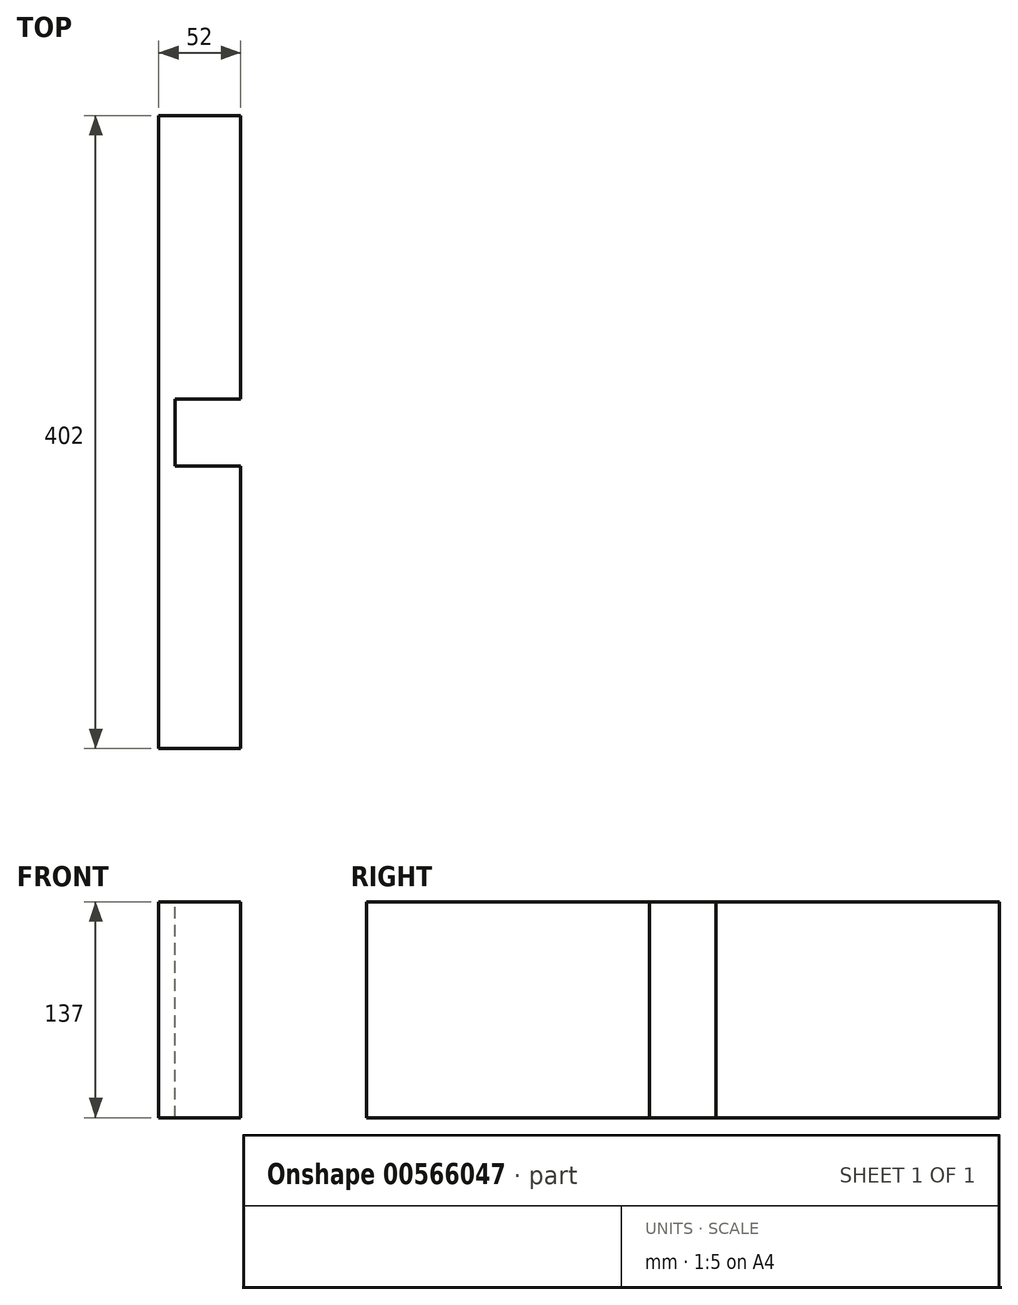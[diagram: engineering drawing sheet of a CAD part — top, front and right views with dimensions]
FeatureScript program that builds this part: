
annotation { "Feature Type Name" : "Feature", "Feature Type Description" : "" }
export const myFeature = defineFeature(function(context is Context, id is Id, definition is map)
    precondition{}
    {
        {
            var Q0;
            Q0=qCreatedBy(makeId("Top.planeOp"),FACE);
            var sketch = newSketch(context, id + "F0", { "sketchPlane" : qUnion([Q0])});
            skLineSegment(sketch, "E0.bottom", {"start": v(-95.63, 172.8) * mm, "end": v(-43.63, 172.8) * mm});
            skLineSegment(sketch, "E0.top", {"start": v(-95.63, -229.2) * mm, "end": v(-43.63, -229.2) * mm});
            skLineSegment(sketch, "E0.left", {"start": v(-95.63, 172.8) * mm, "end": v(-95.63, -229.2) * mm});
            skLineSegment(sketch, "E0.right", {"start": v(-43.63, 172.8) * mm, "end": v(-43.63, -229.2) * mm});
            skSolve(sketch);
        }
        {
            var Q0;
            Q0 = qSketchRegion(id + "F0", true);
            extrude(context, id + "F1", {"entities" : qUnion([Q0]), "depth" : 137 * mm, "offsetDistance" : 25 * mm});
        }
        {
            var Q0;
            Q0=makeQuery(id+"F1.opExtrude","CAP_FACE",FACE,{"disambiguationData":[OSD([sQuery(id+"F0.wireOp",EDGE,"E0.bottom"),sQuery(id+"F0.wireOp",EDGE,"E0.top"),sQuery(id+"F0.wireOp",EDGE,"E0.left"),sQuery(id+"F0.wireOp",EDGE,"E0.right")])],"isStart":false});
            var sketch = newSketch(context, id + "F2", { "sketchPlane" : qUnion([Q0])});
            skLineSegment(sketch, "E1", {"start": v(-43.63, -28.2) * mm, "end": v(-43.63, -7.3) * mm});
            skLineSegment(sketch, "E2", {"start": v(-43.63, -7.3) * mm, "end": v(-85.17, -7.3) * mm});
            skLineSegment(sketch, "E3", {"start": v(-85.17, -7.3) * mm, "end": v(-85.17, -49.66) * mm});
            skLineSegment(sketch, "E4", {"start": v(-85.17, -49.66) * mm, "end": v(-43.63, -49.66) * mm});
            skLineSegment(sketch, "E5", {"start": v(-43.63, -49.66) * mm, "end": v(-43.63, -28.2) * mm});
            skSolve(sketch);
        }
        {
            var Q0;
            Q0 = qSketchRegion(id + "F2", true);
            extrude(context, id + "F3", {"entities" : qUnion([Q0]), "operationType" : NewBodyOperationType.REMOVE, "oppositeDirection" : true, "depth" : 137 * mm, "offsetDistance" : 25 * mm});
        }
    });
